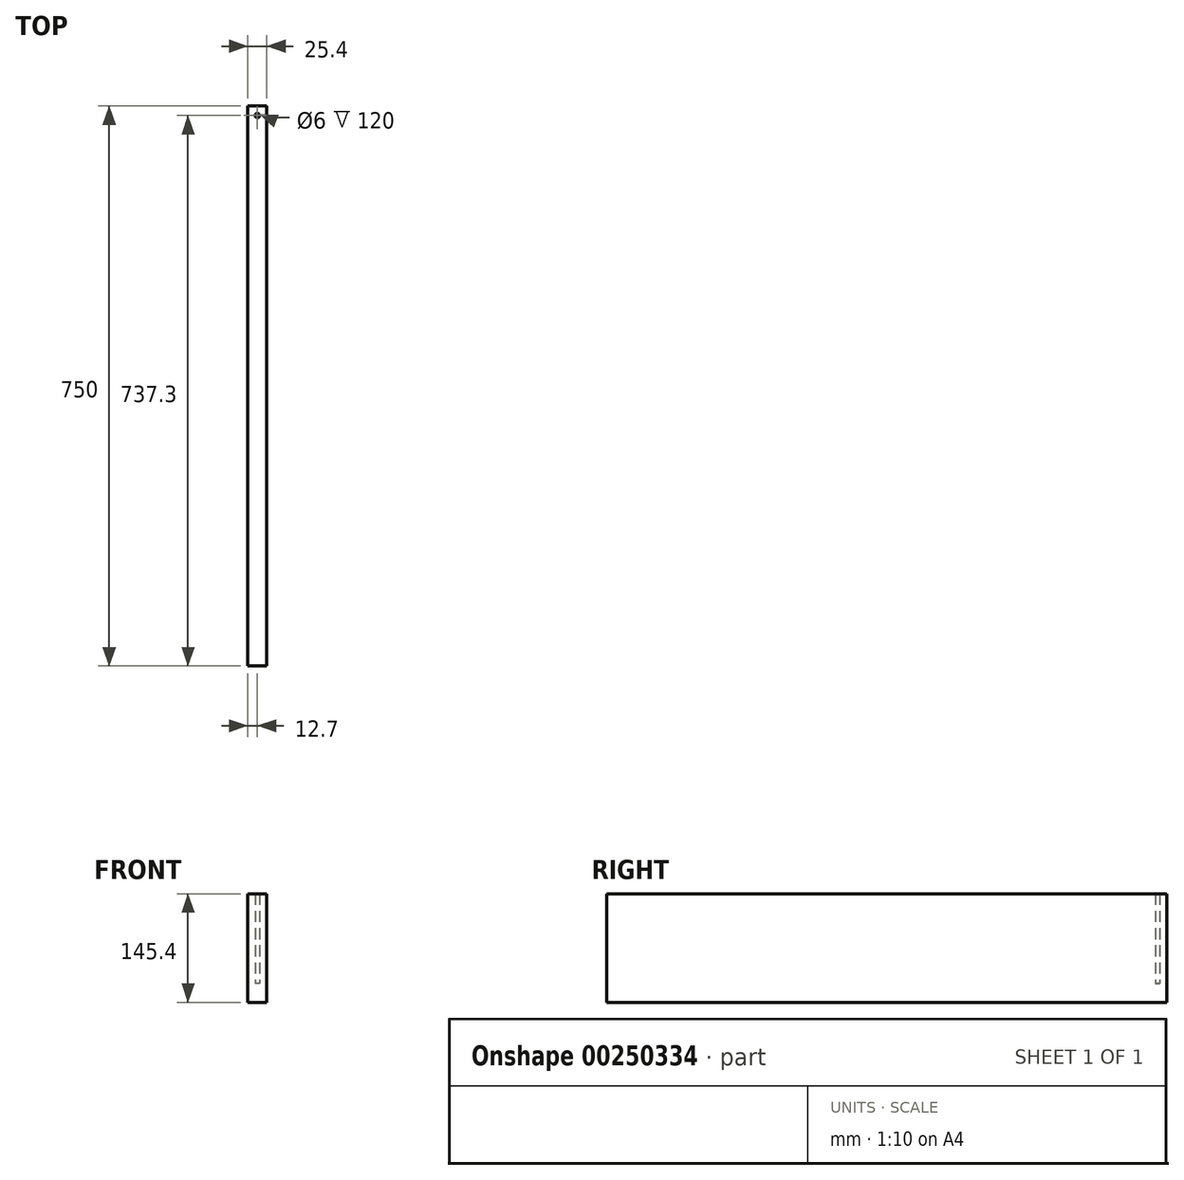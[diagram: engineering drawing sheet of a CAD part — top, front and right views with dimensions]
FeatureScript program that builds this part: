
annotation { "Feature Type Name" : "Feature", "Feature Type Description" : "" }
export const myFeature = defineFeature(function(context is Context, id is Id, definition is map)
    precondition{}
    {
        {
            var Q0;
            Q0=qCreatedBy(makeId("Front.planeOp"),FACE);
            var sketch = newSketch(context, id + "F0", { "sketchPlane" : qUnion([Q0])});
            skLineSegment(sketch, "E0.bottom", {"start": v(12.7, -12.7) * mm, "end": v(-12.7, -12.7) * mm});
            skLineSegment(sketch, "E0.top", {"start": v(12.7, 12.7) * mm, "end": v(-12.7, 12.7) * mm});
            skLineSegment(sketch, "E0.left", {"start": v(12.7, -12.7) * mm, "end": v(12.7, 12.7) * mm});
            skLineSegment(sketch, "E0.right", {"start": v(-12.7, -12.7) * mm, "end": v(-12.7, 12.7) * mm});
            skPoint(sketch, "E0.middle", {"position": v(0, 0) * mm});
            skSolve(sketch);
        }
        {
            var Q0;
            Q0=makeQuery(id+"F0.imprint","IMPRINT",FACE,{"disambiguationData":[TD([[makeQuery(id+"F0.imprint","IMPRINT",EDGE,{"derivedFrom":sQuery(id+"F0.wireOp",EDGE,"E0.bottom")}),-1.0]])]});
            extrude(context, id + "F1", {"entities" : qUnion([Q0]), "endBound" : BoundingType.SYMMETRIC, "depth" : 750 * mm});
        }
        {
            var Q0;
            Q0=makeQuery(id+"F1.opExtrude","SWEPT_FACE",FACE,{"disambiguationData":[OSD([sQuery(id+"F0.wireOp",EDGE,"E0.top")])]});
            var sketch = newSketch(context, id + "F2", { "sketchPlane" : qUnion([Q0])});
            skCircle(sketch, "E1", {"center": v(0, -362.3) * mm, "radius": 3 * mm});
            skPoint(sketch, "E1.centerSnap0", {"position": v(0, -375) * mm});
            skCircle(sketch, "E2.MirrorC", {"center": v(0, 362.3) * mm, "radius": 3 * mm});
            skSolve(sketch);
        }
        {
            var Q0;
            Q0=makeQuery(id+"F0.imprint","IMPRINT",FACE,{"disambiguationData":[TD([[makeQuery(id+"F0.imprint","IMPRINT",EDGE,{"derivedFrom":sQuery(id+"F0.wireOp",EDGE,"E0.bottom")}),-1.0]])]});
            extrude(context, id + "F3", {"entities" : qUnion([Q0]), "endBound" : BoundingType.SYMMETRIC, "depth" : 750 * mm});
        }
        {
            var Q0;
            Q0=makeQuery(id+"F2.imprint","IMPRINT",FACE,{"disambiguationData":[TD([[makeQuery(id+"F2.imprint","IMPRINT",EDGE,{"derivedFrom":sQuery(id+"F2.wireOp",EDGE,"E1")}),1.0]])]});
            var Q1;
            Q1=makeQuery(id+"F2.imprint","IMPRINT",FACE,{"disambiguationData":[TD([[makeQuery(id+"F2.imprint","IMPRINT",EDGE,{"derivedFrom":sQuery(id+"F2.wireOp",EDGE,"E2.MirrorC")}),-1.0]])]});
            extrude(context, id + "F4", {"entities" : qUnion([Q0, Q1]), "operationType" : NewBodyOperationType.ADD, "depth" : 120 * mm});
        }
    });
